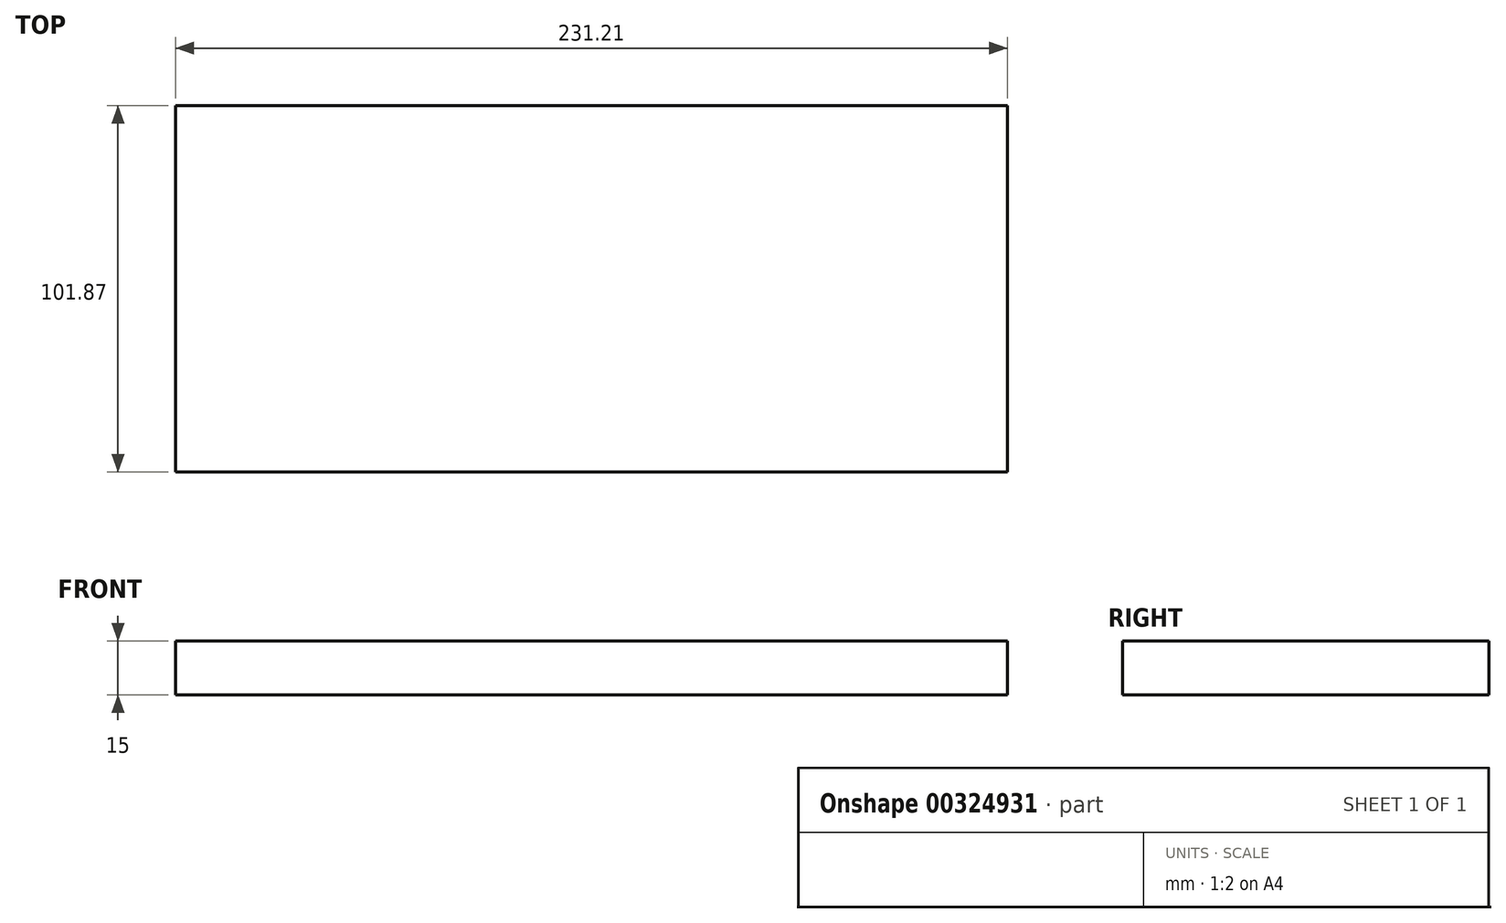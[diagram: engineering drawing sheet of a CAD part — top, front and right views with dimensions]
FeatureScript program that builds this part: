
annotation { "Feature Type Name" : "Feature", "Feature Type Description" : "" }
export const myFeature = defineFeature(function(context is Context, id is Id, definition is map)
    precondition{}
    {
        {
            var Q0;
            Q0=qCreatedBy(makeId("Top.planeOp"),FACE);
            var sketch = newSketch(context, id + "F0", { "sketchPlane" : qUnion([Q0])});
            skLineSegment(sketch, "E0.bottom", {"start": v(-71.88, 52.65) * mm, "end": v(159.33, 52.65) * mm});
            skLineSegment(sketch, "E0.top", {"start": v(-71.88, -49.22) * mm, "end": v(159.33, -49.22) * mm});
            skLineSegment(sketch, "E0.left", {"start": v(-71.88, 52.65) * mm, "end": v(-71.88, -49.22) * mm});
            skLineSegment(sketch, "E0.right", {"start": v(159.33, 52.65) * mm, "end": v(159.33, -49.22) * mm});
            skSolve(sketch);
        }
        {
            var Q0;
            Q0 = qSketchRegion(id + "F0", true);
            extrude(context, id + "F1", {"entities" : qUnion([Q0]), "depth" : 15 * mm});
        }
    });
